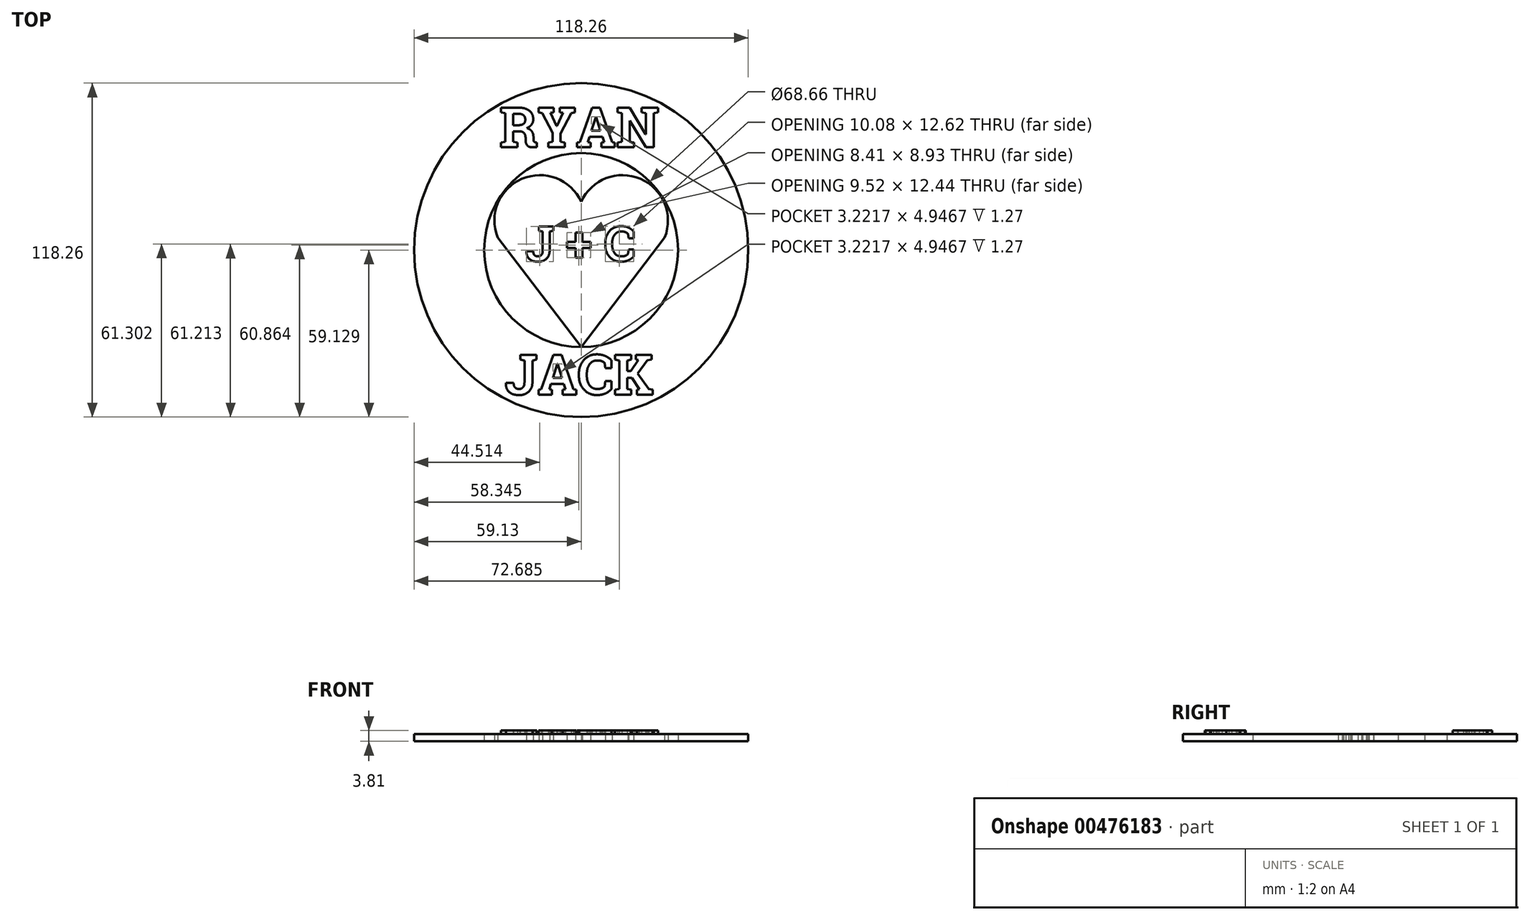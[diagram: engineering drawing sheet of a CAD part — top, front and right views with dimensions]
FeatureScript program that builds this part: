
annotation { "Feature Type Name" : "Feature", "Feature Type Description" : "" }
export const myFeature = defineFeature(function(context is Context, id is Id, definition is map)
    precondition{}
    {
        {
            var Q0;
            Q0=qCreatedBy(makeId("Top.planeOp"),FACE);
            var sketch = newSketch(context, id + "F0", { "sketchPlane" : qUnion([Q0])});
            skArc(sketch, "E0", {"start": v(29.58, -12.65) * mm, "mid": v(20.96, 8.1) * mm, "end": v(0, 0) * mm});
            skCircle(sketch, "E1", {"center": v(0, -17.11) * mm, "radius": 34.33 * mm});
            skCircle(sketch, "E2", {"center": v(0, -17.11) * mm, "radius": 59.13 * mm});
            skLineSegment(sketch, "E3", {"start": v(29.58, -12.65) * mm, "end": v(0, -51.44) * mm});
            skArc(sketch, "E4.MirrorCS", {"start": v(-29.58, -12.65) * mm, "mid": v(-20.96, 8.1) * mm, "end": v(0, 0) * mm});
            skLineSegment(sketch, "E5", {"start": v(-29.58, -12.65) * mm, "end": v(0, -51.44) * mm});
            skText(sketch, "E6", { "text": "J + C", "fontName": "RobotoSlab-Bold.ttf"});
            const initialGuessF0  = {"E6": [-0.01967, -0.02107, 1, 0, 0.01242]};
            skSetInitialGuess(sketch, initialGuessF0);
            skSolve(sketch);
        }
        {
            var Q0;
            Q0=makeQuery(id+"F0.imprint","IMPRINT",FACE,{"disambiguationData":[TD([[makeQuery(id+"F0.imprint","IMPRINT",EDGE,{"derivedFrom":sQuery(id+"F0.wireOp",EDGE,"E1")}),-1.0]])]});
            var Q1;
            Q1=makeQuery(id+"F0.imprint","IMPRINT",FACE,{"disambiguationData":[TD([[makeQuery(id+"F0.imprint","IMPRINT",EDGE,{"derivedFrom":sQuery(id+"F0.wireOp",EDGE,"E0")}),1.0]])]});
            extrude(context, id + "F1", {"entities" : qUnion([Q0, Q1]), "depth" : 2.54 * mm});
        }
        {
            var Q0;
            Q0=makeQuery(id+"F1.opExtrude","CAP_FACE",FACE,{"disambiguationData":[OSD([sQuery(id+"F0.wireOp",EDGE,"E1"),sQuery(id+"F0.wireOp",EDGE,"E2")])],"isStart":false});
            var sketch = newSketch(context, id + "F2", { "sketchPlane" : qUnion([Q0])});
            skText(sketch, "E7", { "text": "RYAN", "fontName": "RobotoSlab-Bold.ttf"});
            skText(sketch, "E8", { "text": "JACK", "fontName": "RobotoSlab-Bold.ttf"});
            const initialGuessF2  = {"E7": [-0.02893, 0.01926, 1, 0, 0.01422], "E8": [-0.027, -0.06827, 1, 0, 0.01422]};
            skSetInitialGuess(sketch, initialGuessF2);
            skSolve(sketch);
        }
        {
            var Q0;
            Q0 = qSketchRegion(id + "F2", true);
            extrude(context, id + "F3", {"entities" : qUnion([Q0]), "operationType" : NewBodyOperationType.ADD, "depth" : 1.27 * mm});
        }
    });
